# Revit family: Spaces In Between_Collaborate
name_source: partatom
category: Furniture
units: mm (PartAtom-declared; Revit-internal decimal feet)

## family parameters
Always vertical = Yes
Cut with Voids When Loaded = No
OmniClass Number = 23.40.20.00
OmniClass Title = General Furniture and Specialties
Room Calculation Point = No
Shared = No
Work Plane-Based = No

## types (1)
- Spaces In Between_Collaborate
    14"H Ottoman HPL Edge 1 = <By Category>
    14"H Ottoman HPL Edge 2 = <By Category>
    14"H Ottoman HPL Top 1 = <By Category>
    14"H Ottoman HPL Top 2 = <By Category>
    14"H Ottoman Seat 1 = <By Category>
    14"H Ottoman Seat 2 = <By Category>
    14"H Ottoman Side 1 = <By Category>
    14"H Ottoman Side 2 = <By Category>
    16"H Ottoman HPL  Edge 2 = <By Category>
    16"H Ottoman HPL Edge 1 = <By Category>
    16"H Ottoman HPL Top 1 = <By Category>
    16"H Ottoman HPL Top 2 = <By Category>
    16"H Ottoman Seat 1 = <By Category>
    16"H Ottoman Seat 2 = <By Category>
    16"H Ottoman Side 1 = <By Category>
    16"H Ottoman Side 2 = <By Category>
    18"H Ottoman HPL Edge 1 = <By Category>
    18"H Ottoman HPL Edge 2 = <By Category>
    18"H Ottoman HPL Top 1 = <By Category>
    18"H Ottoman HPL Top 2 = <By Category>
    18"H Ottoman Seat 1 = <By Category>
    18"H Ottoman Seat 2 = <By Category>
    18"H Ottoman Side 1 = <By Category>
    18"H Ottoman Side 2 = <By Category>
    3" Rectangle Leg = <By Category>
    6" Rectangle Leg = <By Category>
    Chair Back Fabric 1 = <By Category>
    Chair Back Fabric 2 = <By Category>
    Chair Back Fabric 3 = <By Category>
    Chair Back Fabric 4 = <By Category>
    Chair Back Fabric 5 = <By Category>
    Chair Back Fabric 6 = <By Category>
    Chair Seat Fabric 1 = <By Category>
    Chair Seat Fabric 2 = <By Category>
    Chair Seat Fabric 3 = <By Category>
    Chair Seat Fabric 4 = <By Category>
    Chair Seat Fabric 5 = <By Category>
    Chair Seat Fabric 6 = <By Category>
    Glide = <By Category>
    Manufacturer = FOMCORE
    Model = Spaces In Between_Collaborate
    Sled Leg29 = <By Category>
    Triangle Leg = <By Category>
    Type Comments = COMBO UNIT
    URL = https://fomcore.com
    Wedge Seat 1 = <By Category>
    Wedge Seat 2 = <By Category>
    Wedge Seat 3 = <By Category>
    Wedge Seat 4 = <By Category>
    Wedge Side 1 = <By Category>
    Wedge Side 2 = <By Category>
    Wedge Side 3 = <By Category>
    Wedge Side 4 = <By Category>

## geometry (parser evidence)
native form markers: Sweep x3
no freeform markers — native parametric forms only
